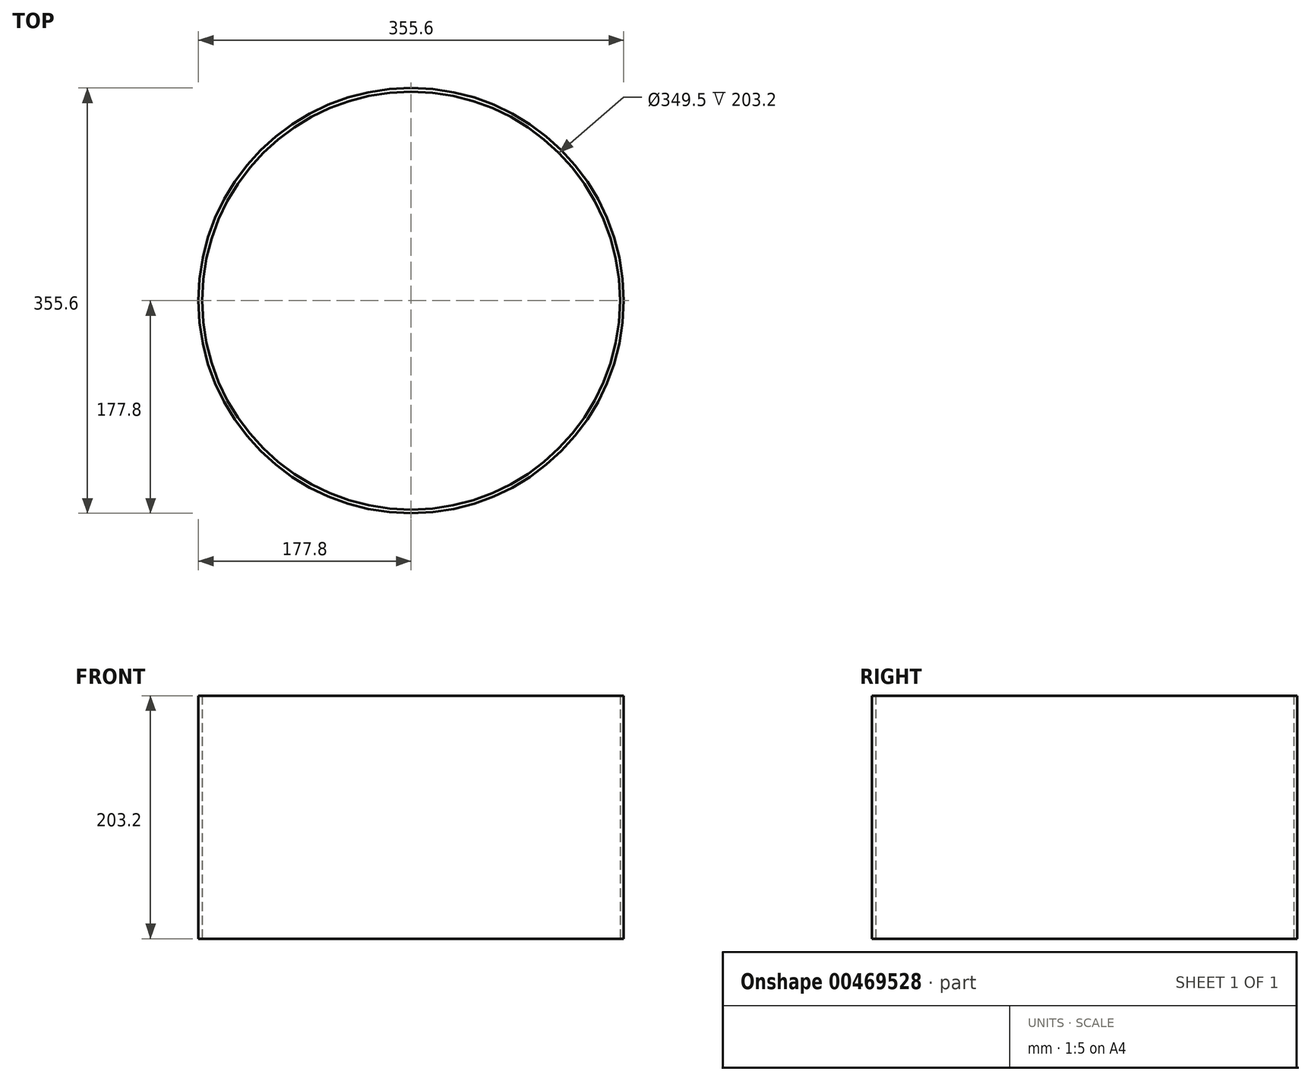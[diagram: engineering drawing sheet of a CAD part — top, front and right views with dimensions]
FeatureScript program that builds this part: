
annotation { "Feature Type Name" : "Feature", "Feature Type Description" : "" }
export const myFeature = defineFeature(function(context is Context, id is Id, definition is map)
    precondition{}
    {
        {
            var Q0;
            Q0=qCreatedBy(makeId("Top.planeOp"),FACE);
            var sketch = newSketch(context, id + "F0", { "sketchPlane" : qUnion([Q0])});
            skCircle(sketch, "E0", {"center": v(0, 0) * mm, "radius": 174.75 * mm});
            skCircle(sketch, "E1", {"center": v(0, 0) * mm, "radius": 177.8 * mm});
            skSolve(sketch);
        }
        {
            var Q0;
            Q0 = qSketchRegion(id + "F0", true);
            extrude(context, id + "F1", {"entities" : qUnion([Q0]), "depth" : 203.2 * mm, "offsetDistance" : 25.4 * mm});
        }
    });
